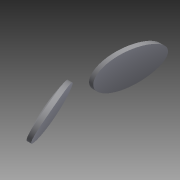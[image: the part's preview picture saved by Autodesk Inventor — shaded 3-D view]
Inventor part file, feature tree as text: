
AUTODESK INVENTOR PART (.ipt)
format: ipt  version: 2015 (Build 190159000, 159)  size: 119,808 bytes
history: native  units: in
note: dims shown in document units (in); Inventor stores cm internally (conversion verified against a paired STEP export)
features: sketch x4, reference x4, revolve x2, plane x1, extrude x1
ambient origin geometry x8: Origin, YZ Plane, XZ Plane, XY Plane, X Axis, Y Axis, Z Axis, Center Point
bodies: Solid1 (feature_tree)
feature tree (12):
  sketch  "Sketch1"  dims[d1=0.2in d2=0.2in]
  plane  "Work Plane1"
  extrude  "Extrusion1"  Depth=0.2in
  revolve  "Revolution1"  [1 undecoded]
  revolve  "Revolution2"  [1 undecoded]
  reference  "Reference1"
  sketch  "Sketch2"  dims[d3=0.35in d4=0.2in d5=0.0in]
  reference  "Reference2"
  reference  "Reference3"
  sketch  "Sketch3"  dims[d6=90.0deg d7=0.02in]
  reference  "Reference4"
  sketch  "Sketch4"  dims[d8=0.015in d9=90.0deg]
note: 2 required parameter values undecoded (feature->parameter linkage not recoverable at this tier; creation-order binding heuristic only, values carry confidence <= 0.55)
